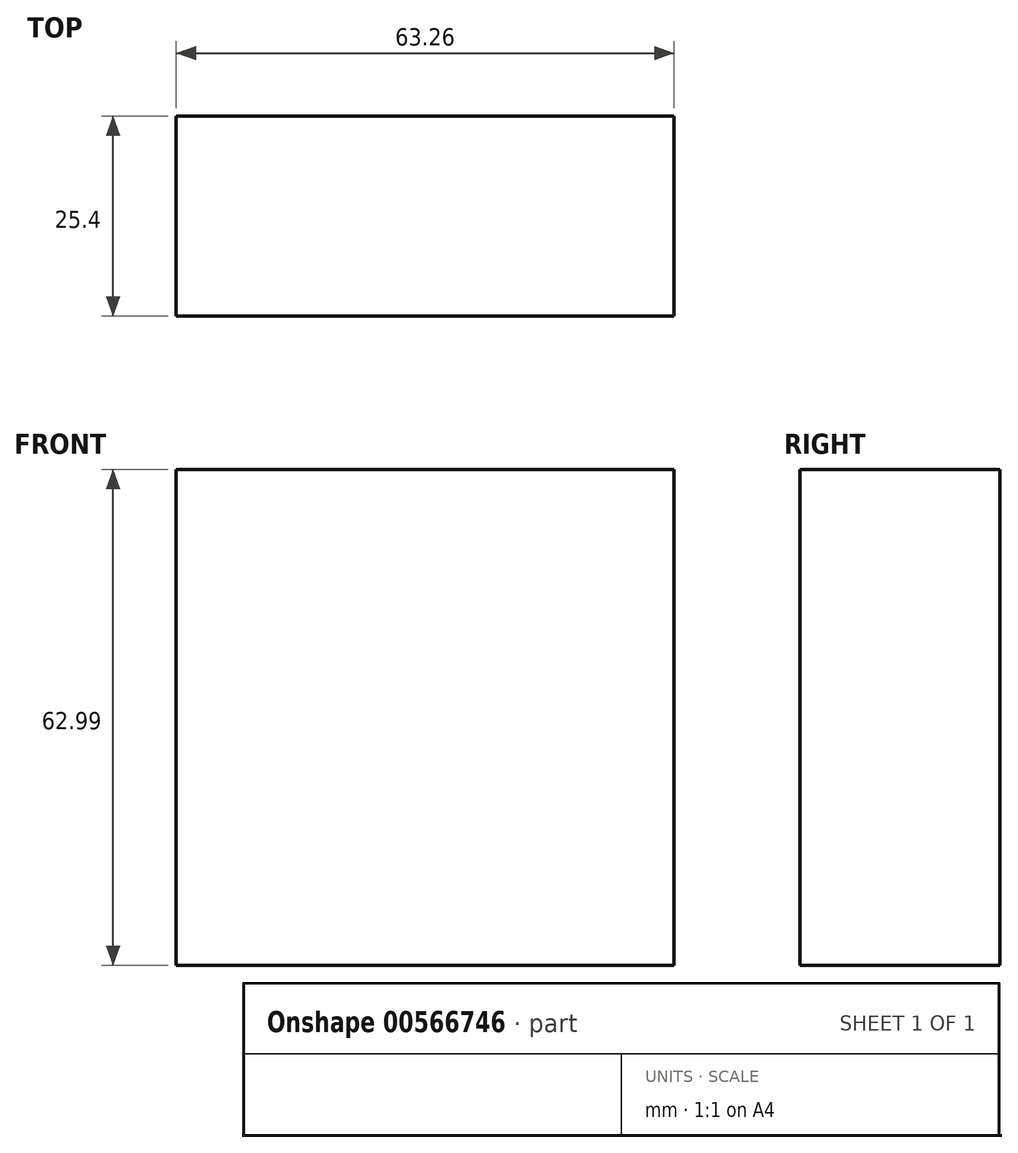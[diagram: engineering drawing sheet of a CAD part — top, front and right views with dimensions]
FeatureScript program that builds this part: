
annotation { "Feature Type Name" : "Feature", "Feature Type Description" : "" }
export const myFeature = defineFeature(function(context is Context, id is Id, definition is map)
    precondition{}
    {
        {
            var Q0;
            Q0=qCreatedBy(makeId("Front.planeOp"),FACE);
            var sketch = newSketch(context, id + "F0", { "sketchPlane" : qUnion([Q0])});
            skLineSegment(sketch, "E0.bottom", {"start": v(-38.31, 28.1) * mm, "end": v(24.95, 28.1) * mm});
            skLineSegment(sketch, "E0.top", {"start": v(-38.31, -34.89) * mm, "end": v(24.95, -34.89) * mm});
            skLineSegment(sketch, "E0.left", {"start": v(-38.31, 28.1) * mm, "end": v(-38.31, -34.89) * mm});
            skLineSegment(sketch, "E0.right", {"start": v(24.95, 28.1) * mm, "end": v(24.95, -34.89) * mm});
            skSolve(sketch);
        }
        {
            var Q0;
            Q0=makeQuery(id+"F0.imprint","IMPRINT",FACE,{"disambiguationData":[TD([[makeQuery(id+"F0.imprint","IMPRINT",EDGE,{"derivedFrom":sQuery(id+"F0.wireOp",EDGE,"E0.bottom")}),-1.0]])]});
            extrude(context, id + "F1", {"entities" : qUnion([Q0]), "depth" : 25.4 * mm, "offsetDistance" : 25.4 * mm});
        }
    });
